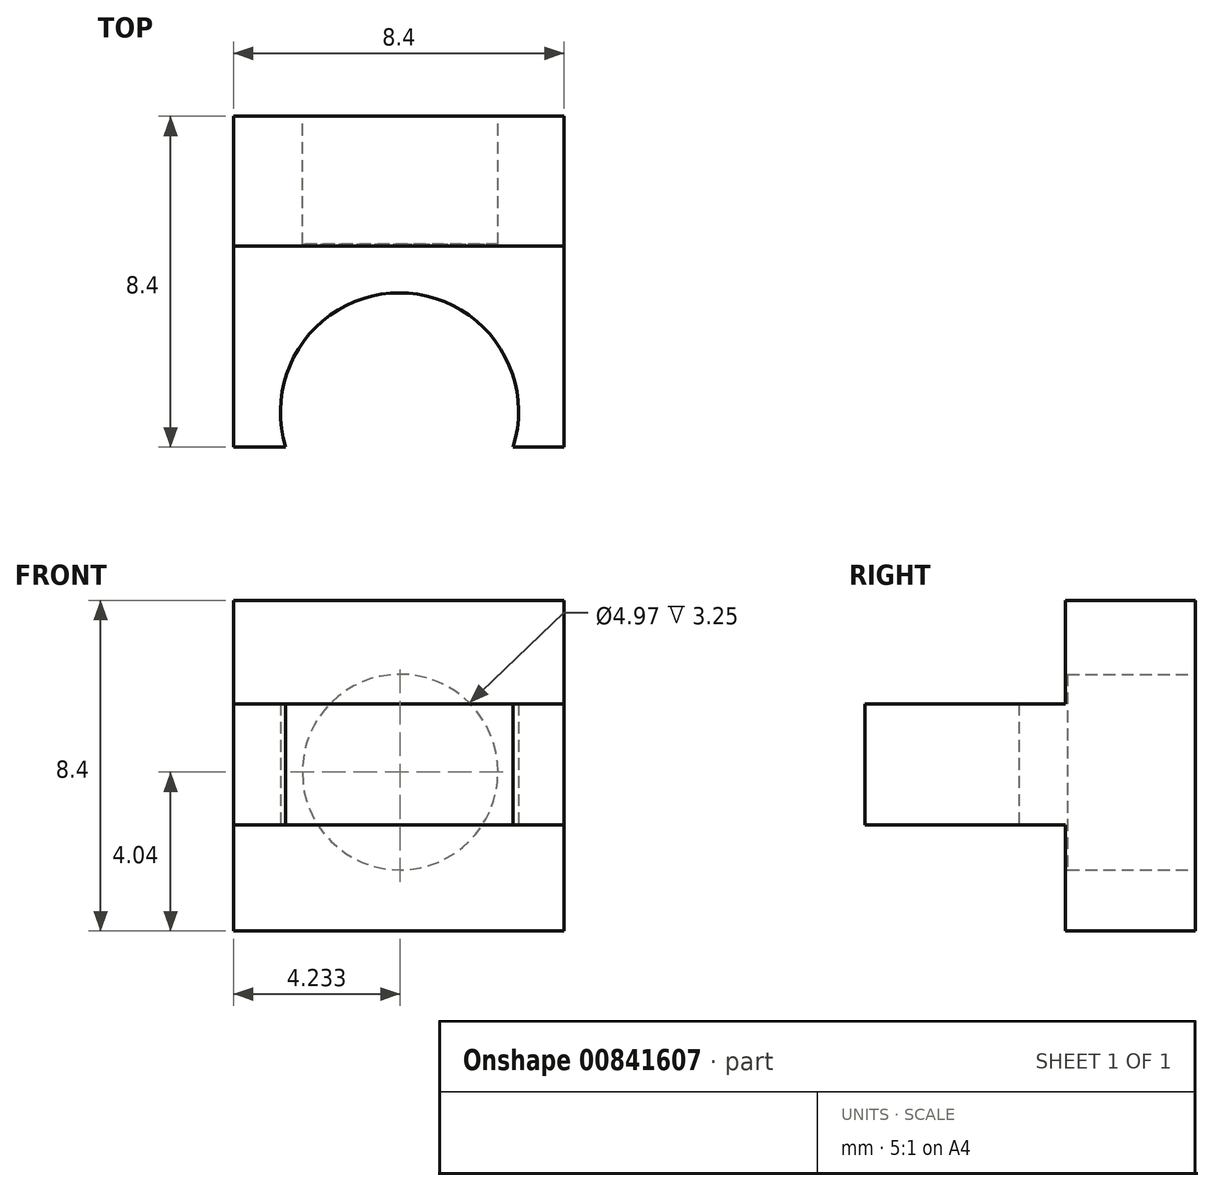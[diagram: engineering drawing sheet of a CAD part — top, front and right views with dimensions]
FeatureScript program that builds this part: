
annotation { "Feature Type Name" : "Feature", "Feature Type Description" : "" }
export const myFeature = defineFeature(function(context is Context, id is Id, definition is map)
    precondition{}
    {
        {
            var Q0;
            Q0=qCreatedBy(makeId("Front.planeOp"),FACE);
            var sketch = newSketch(context, id + "F0", { "sketchPlane" : qUnion([Q0])});
            skLineSegment(sketch, "E0", {"start": v(-8.4, 4.36) * mm, "end": v(-8.4, -4.04) * mm});
            skLineSegment(sketch, "E1", {"start": v(-8.4, -4.04) * mm, "end": v(0, -4.04) * mm});
            skLineSegment(sketch, "E2", {"start": v(0, -4.04) * mm, "end": v(0, 4.36) * mm});
            skLineSegment(sketch, "E3", {"start": v(0, 4.36) * mm, "end": v(-8.4, 4.36) * mm});
            skSolve(sketch);
        }
        {
            var Q0;
            Q0=qSketchRegion(id+"F0",true);
            extrude(context, id + "F1", {"entities" : qUnion([Q0]), "depth" : 3.3 * mm, "offsetDistance" : 25 * mm});
        }
        {
            var Q0;
            Q0=makeQuery(id+"F1.opExtrude","CAP_FACE",FACE,{"disambiguationData":[OSD([sQuery(id+"F0.wireOp",EDGE,"E0"),sQuery(id+"F0.wireOp",EDGE,"E1"),sQuery(id+"F0.wireOp",EDGE,"E2"),sQuery(id+"F0.wireOp",EDGE,"E3")])],"isStart":false});
            var sketch = newSketch(context, id + "F2", { "sketchPlane" : qUnion([Q0])});
            skLineSegment(sketch, "E4", {"start": v(-8.4, 1.74) * mm, "end": v(-8.4, -1.34) * mm});
            skLineSegment(sketch, "E5", {"start": v(-8.4, -1.34) * mm, "end": v(0, -1.34) * mm});
            skLineSegment(sketch, "E6", {"start": v(0, -1.34) * mm, "end": v(0, 1.74) * mm});
            skLineSegment(sketch, "E7", {"start": v(0, 1.74) * mm, "end": v(-8.4, 1.74) * mm});
            skSolve(sketch);
        }
        {
            var Q0;
            Q0=qSketchRegion(id+"F2",true);
            extrude(context, id + "F3", {"entities" : qUnion([Q0]), "operationType" : NewBodyOperationType.ADD, "depth" : 5.1 * mm, "offsetDistance" : 25 * mm});
        }
        {
            var Q0;
            Q0=makeQuery(id+"F3.opExtrude","SWEPT_FACE",FACE,{"disambiguationData":[OSD([sQuery(id+"F2.wireOp",EDGE,"E5")])]});
            var sketch = newSketch(context, id + "F4", { "sketchPlane" : qUnion([Q0])});
            skArc(sketch, "E8", {"start": v(-7.07, 8.4) * mm, "mid": v(-4.18, 4.48) * mm, "end": v(-1.3, 8.4) * mm});
            skSolve(sketch);
        }
        {
            var Q0;
            Q0=qSketchRegion(id+"F4",true);
            var Q1;
            {var subQ0=sQuery(id+"F4.wireOp",EDGE,"E8");Q1=makeQuery(id+"F4.imprint","IMPRINT",FACE,{"disambiguationData":[TD([[makeQuery(id+"F4.imprint","IMPRINT",EDGE,{"derivedFrom":subQ0}),1.0]])]});}
            extrude(context, id + "F5", {"entities" : qUnion([Q0, Q1]), "operationType" : NewBodyOperationType.REMOVE, "oppositeDirection" : true, "depth" : 25 * mm, "offsetDistance" : 25 * mm});
        }
        {
            var Q0;
            Q0=makeQuery(id+"F1.opExtrude","CAP_FACE",FACE,{"disambiguationData":[OSD([sQuery(id+"F0.wireOp",EDGE,"E0"),sQuery(id+"F0.wireOp",EDGE,"E1"),sQuery(id+"F0.wireOp",EDGE,"E2"),sQuery(id+"F0.wireOp",EDGE,"E3")])],"isStart":true});
            var sketch = newSketch(context, id + "F6", { "sketchPlane" : qUnion([Q0])});
            skCircle(sketch, "E9", {"center": v(4.17, 0) * mm, "radius": 2.48 * mm});
            skSolve(sketch);
        }
        {
            var Q0;
            Q0=qSketchRegion(id+"F6",true);
            extrude(context, id + "F7", {"entities" : qUnion([Q0]), "operationType" : NewBodyOperationType.REMOVE, "oppositeDirection" : true, "depth" : 3.25 * mm, "offsetDistance" : 25 * mm});
        }
    });
